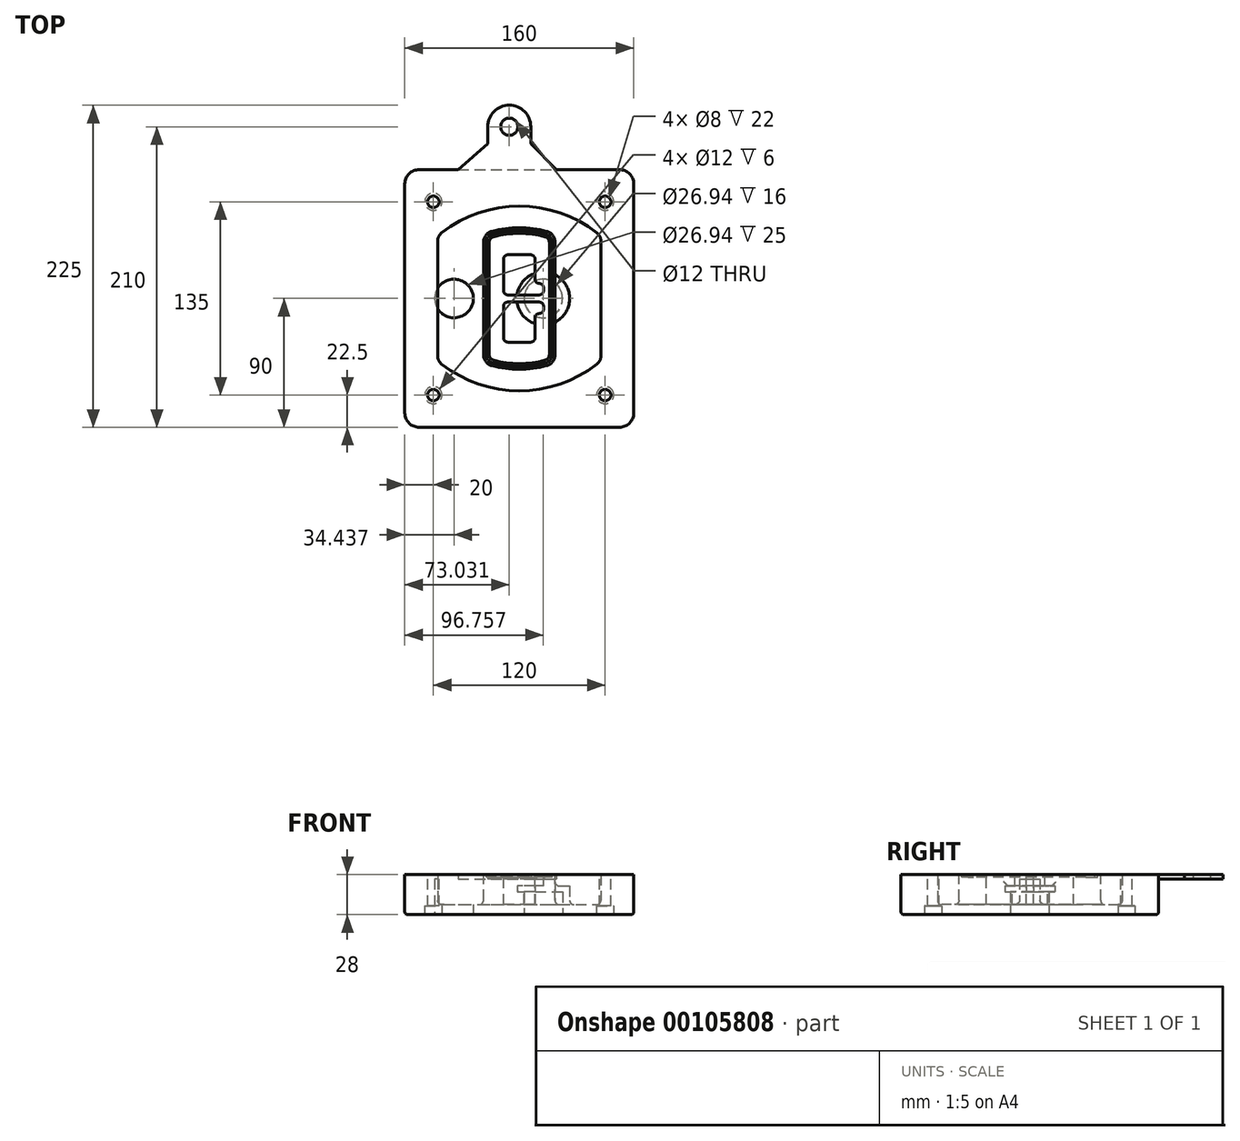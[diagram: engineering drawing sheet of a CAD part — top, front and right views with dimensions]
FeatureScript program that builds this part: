
annotation { "Feature Type Name" : "Feature", "Feature Type Description" : "" }
export const myFeature = defineFeature(function(context is Context, id is Id, definition is map)
    precondition{}
    {
        {
            var Q0;
            Q0=qCreatedBy(makeId("Top.planeOp"),FACE);
            var sketch = newSketch(context, id + "F0", { "sketchPlane" : qUnion([Q0])});
            skPoint(sketch, "E0.rect.middle", {"position": v(0, 0) * mm});
            skLineSegment(sketch, "E1.bottom", {"start": v(-70, -90) * mm, "end": v(70, -90) * mm});
            skLineSegment(sketch, "E1.top", {"start": v(-70, 90) * mm, "end": v(70, 90) * mm});
            skLineSegment(sketch, "E1.left", {"start": v(-80, -80) * mm, "end": v(-80, 80) * mm});
            skLineSegment(sketch, "E1.right", {"start": v(80, -80) * mm, "end": v(80, 80) * mm});
            skLineSegment(sketch, "E2", {"start": v(-80, 90) * mm, "end": v(80, -90) * mm, "construction": true});
            skLineSegment(sketch, "E3", {"start": v(80, 90) * mm, "end": v(-80, -90) * mm, "construction": true});
            skCircle(sketch, "E4", {"center": v(-60, 67.5) * mm, "radius": 4 * mm});
            skCircle(sketch, "E5", {"center": v(60, 67.5) * mm, "radius": 4 * mm});
            skCircle(sketch, "E6", {"center": v(60, -67.5) * mm, "radius": 4 * mm});
            skCircle(sketch, "E7", {"center": v(-60, -67.5) * mm, "radius": 4 * mm});
            skLineSegment(sketch, "E8", {"start": v(-60, 67.5) * mm, "end": v(60, 67.5) * mm, "construction": true});
            skLineSegment(sketch, "E9", {"start": v(60, 67.5) * mm, "end": v(60, -67.5) * mm, "construction": true});
            skLineSegment(sketch, "E10", {"start": v(60, -67.5) * mm, "end": v(-60, -67.5) * mm, "construction": true});
            skLineSegment(sketch, "E11", {"start": v(-60, -67.5) * mm, "end": v(-60, 67.5) * mm, "construction": true});
            skLineSegment(sketch, "E12", {"start": v(-60, 40.3) * mm, "end": v(-60, -40.3) * mm});
            skLineSegment(sketch, "E13", {"start": v(60, 40.3) * mm, "end": v(60, -40.3) * mm});
            skArc(sketch, "E14", {"start": v(56.15, 48.18) * mm, "mid": v(0, 67.5) * mm, "end": v(-56.15, 48.18) * mm});
            skArc(sketch, "E15", {"start": v(-56.15, -48.18) * mm, "mid": v(0, -67.5) * mm, "end": v(56.15, -48.18) * mm});
            skLineSegment(sketch, "E16", {"start": v(-60, 0) * mm, "end": v(60, 0) * mm, "construction": true});
            skPoint(sketch, "E17.visualSharp", {"position": v(-60, -45) * mm});
            skArc(sketch, "E17.filletArc", {"start": v(-60, -40.3) * mm, "mid": v(-58.99, -44.68) * mm, "end": v(-56.15, -48.18) * mm});
            skPoint(sketch, "E18.visualSharp", {"position": v(-60, 45) * mm});
            skArc(sketch, "E18.filletArc", {"start": v(-56.15, 48.18) * mm, "mid": v(-58.99, 44.68) * mm, "end": v(-60, 40.3) * mm});
            skPoint(sketch, "E19.visualSharp", {"position": v(60, 45) * mm});
            skArc(sketch, "E19.filletArc", {"start": v(60, 40.3) * mm, "mid": v(58.99, 44.68) * mm, "end": v(56.15, 48.18) * mm});
            skPoint(sketch, "E20.visualSharp", {"position": v(60, -45) * mm});
            skArc(sketch, "E20.filletArc", {"start": v(56.15, -48.18) * mm, "mid": v(58.99, -44.68) * mm, "end": v(60, -40.3) * mm});
            skPoint(sketch, "E21.visualSharp", {"position": v(-80, 90) * mm});
            skArc(sketch, "E21.filletArc", {"start": v(-70, 90) * mm, "mid": v(-77.07, 87.07) * mm, "end": v(-80, 80) * mm});
            skPoint(sketch, "E22.visualSharp", {"position": v(80, 90) * mm});
            skArc(sketch, "E22.filletArc", {"start": v(80, 80) * mm, "mid": v(77.07, 87.07) * mm, "end": v(70, 90) * mm});
            skPoint(sketch, "E23.visualSharp", {"position": v(80, -90) * mm});
            skArc(sketch, "E23.filletArc", {"start": v(70, -90) * mm, "mid": v(77.07, -87.07) * mm, "end": v(80, -80) * mm});
            skPoint(sketch, "E24.visualSharp", {"position": v(-80, -90) * mm});
            skArc(sketch, "E24.filletArc", {"start": v(-80, -80) * mm, "mid": v(-77.07, -87.07) * mm, "end": v(-70, -90) * mm});
            skArc(sketch, "E25.0", {"start": v(57, 40.3) * mm, "mid": v(56.3, 43.36) * mm, "end": v(54.3, 45.81) * mm});
            skLineSegment(sketch, "E25.1", {"start": v(57, 40.3) * mm, "end": v(57, -40.3) * mm});
            skArc(sketch, "E25.2", {"start": v(54.3, -45.81) * mm, "mid": v(56.3, -43.36) * mm, "end": v(57, -40.3) * mm});
            skArc(sketch, "E25.3", {"start": v(-54.3, -45.81) * mm, "mid": v(0, -64.5) * mm, "end": v(54.3, -45.81) * mm});
            skArc(sketch, "E25.4", {"start": v(-57, -40.3) * mm, "mid": v(-56.3, -43.36) * mm, "end": v(-54.3, -45.81) * mm});
            skArc(sketch, "E25.5", {"start": v(54.3, 45.81) * mm, "mid": v(0, 64.5) * mm, "end": v(-54.3, 45.81) * mm});
            skLineSegment(sketch, "E25.6", {"start": v(-57, 40.3) * mm, "end": v(-57, -40.3) * mm});
            skArc(sketch, "E25.7", {"start": v(-54.3, 45.81) * mm, "mid": v(-56.3, 43.36) * mm, "end": v(-57, 40.3) * mm});
            skArc(sketch, "E26.0", {"start": v(-58.62, 51.33) * mm, "mid": v(-62.58, 46.43) * mm, "end": v(-64, 40.3) * mm});
            skArc(sketch, "E26.1", {"start": v(58.62, 51.33) * mm, "mid": v(0, 71.5) * mm, "end": v(-58.62, 51.33) * mm});
            skArc(sketch, "E26.2", {"start": v(64, 40.3) * mm, "mid": v(62.58, 46.43) * mm, "end": v(58.62, 51.33) * mm});
            skLineSegment(sketch, "E26.3", {"start": v(64, 40.3) * mm, "end": v(64, -40.3) * mm});
            skArc(sketch, "E26.4", {"start": v(58.62, -51.33) * mm, "mid": v(62.58, -46.43) * mm, "end": v(64, -40.3) * mm});
            skLineSegment(sketch, "E26.5", {"start": v(-64, 40.3) * mm, "end": v(-64, -40.3) * mm});
            skArc(sketch, "E26.6", {"start": v(-58.62, -51.33) * mm, "mid": v(0, -71.5) * mm, "end": v(58.62, -51.33) * mm});
            skArc(sketch, "E26.7", {"start": v(-64, -40.3) * mm, "mid": v(-62.58, -46.43) * mm, "end": v(-58.62, -51.33) * mm});
            skSolve(sketch);
        }
        {
            var Q0;
            Q0=makeQuery(id+"F0.imprint","IMPRINT",FACE,{"disambiguationData":[TD([[makeQuery(id+"F0.imprint","IMPRINT",EDGE,{"derivedFrom":sQuery(id+"F0.wireOp",EDGE,"E1.bottom")}),1.0]])]});
            var Q1;
            Q1=makeQuery(id+"F0.imprint","IMPRINT",FACE,{"disambiguationData":[TD([[makeQuery(id+"F0.imprint","IMPRINT",EDGE,{"derivedFrom":sQuery(id+"F0.wireOp",EDGE,"E12")}),1.0]])]});
            var Q2;
            Q2=makeQuery(id+"F0.imprint","IMPRINT",FACE,{"disambiguationData":[TD([[makeQuery(id+"F0.imprint","IMPRINT",EDGE,{"derivedFrom":sQuery(id+"F0.wireOp",EDGE,"E25.0")}),1.0]])]});
            var Q3;
            Q3=makeQuery(id+"F0.imprint","IMPRINT",FACE,{"disambiguationData":[TD([[makeQuery(id+"F0.imprint","IMPRINT",EDGE,{"derivedFrom":sQuery(id+"F0.wireOp",EDGE,"E12")}),-1.0]])]});
            extrude(context, id + "F1", {"entities" : qUnion([Q0, Q1, Q2, Q3]), "oppositeDirection" : true, "depth" : 25 * mm});
        }
        {
            var Q0;
            Q0=makeQuery(id+"F0.imprint","IMPRINT",FACE,{"disambiguationData":[TD([[makeQuery(id+"F0.imprint","IMPRINT",EDGE,{"derivedFrom":sQuery(id+"F0.wireOp",EDGE,"E12")}),1.0]])]});
            extrude(context, id + "F2", {"entities" : qUnion([Q0]), "operationType" : NewBodyOperationType.ADD, "depth" : 3 * mm});
        }
        {
            var Q0;
            Q0=makeQuery(id+"F0.imprint","IMPRINT",FACE,{"disambiguationData":[TD([[makeQuery(id+"F0.imprint","IMPRINT",EDGE,{"derivedFrom":sQuery(id+"F0.wireOp",EDGE,"E25.0")}),1.0]])]});
            extrude(context, id + "F3", {"entities" : qUnion([Q0]), "operationType" : NewBodyOperationType.REMOVE, "oppositeDirection" : true, "depth" : 18 * mm});
        }
        {
            var Q0;
            Q0=makeQuery(id+"F2.opExtrude","CAP_FACE",FACE,{"disambiguationData":[OSD([sQuery(id+"F0.wireOp",EDGE,"E12"),sQuery(id+"F0.wireOp",EDGE,"E13"),sQuery(id+"F0.wireOp",EDGE,"E14"),sQuery(id+"F0.wireOp",EDGE,"E15"),sQuery(id+"F0.wireOp",EDGE,"E17.filletArc"),sQuery(id+"F0.wireOp",EDGE,"E18.filletArc"),sQuery(id+"F0.wireOp",EDGE,"E19.filletArc"),sQuery(id+"F0.wireOp",EDGE,"E20.filletArc"),sQuery(id+"F0.wireOp",EDGE,"E25.0"),sQuery(id+"F0.wireOp",EDGE,"E25.1"),sQuery(id+"F0.wireOp",EDGE,"E25.2"),sQuery(id+"F0.wireOp",EDGE,"E25.3"),sQuery(id+"F0.wireOp",EDGE,"E25.4"),sQuery(id+"F0.wireOp",EDGE,"E25.5"),sQuery(id+"F0.wireOp",EDGE,"E25.6"),sQuery(id+"F0.wireOp",EDGE,"E25.7")])],"isStart":false});
            var sketch = newSketch(context, id + "F4", { "sketchPlane" : qUnion([Q0])});
            skArc(sketch, "E27.0", {"start": v(-19.08, -46.97) * mm, "mid": v(0, -49.5) * mm, "end": v(19.08, -46.97) * mm});
            skArc(sketch, "E28.0", {"start": v(19.08, 46.97) * mm, "mid": v(0, 49.5) * mm, "end": v(-19.08, 46.97) * mm});
            skLineSegment(sketch, "E29", {"start": v(-25, 39.25) * mm, "end": v(-25, -39.25) * mm});
            skLineSegment(sketch, "E30", {"start": v(25, 39.25) * mm, "end": v(25, -39.25) * mm});
            skLineSegment(sketch, "E31", {"start": v(-25, 45.1) * mm, "end": v(25, 45.1) * mm, "construction": true});
            skLineSegment(sketch, "E32", {"start": v(-25, -45.1) * mm, "end": v(25, -45.1) * mm, "construction": true});
            skPoint(sketch, "E33.visualSharp", {"position": v(-25, 45.1) * mm});
            skArc(sketch, "E33.filletArc", {"start": v(-19.08, 46.97) * mm, "mid": v(-23.35, 44.11) * mm, "end": v(-25, 39.25) * mm});
            skPoint(sketch, "E34.visualSharp", {"position": v(25, 45.1) * mm});
            skArc(sketch, "E34.filletArc", {"start": v(25, 39.25) * mm, "mid": v(23.35, 44.11) * mm, "end": v(19.08, 46.97) * mm});
            skPoint(sketch, "E35.visualSharp", {"position": v(25, -45.1) * mm});
            skArc(sketch, "E35.filletArc", {"start": v(19.08, -46.97) * mm, "mid": v(23.35, -44.11) * mm, "end": v(25, -39.25) * mm});
            skPoint(sketch, "E36.visualSharp", {"position": v(-25, -45.1) * mm});
            skArc(sketch, "E36.filletArc", {"start": v(-25, -39.25) * mm, "mid": v(-23.35, -44.11) * mm, "end": v(-19.08, -46.97) * mm});
            skArc(sketch, "E37.0", {"start": v(54.3, 45.81) * mm, "mid": v(0, 64.5) * mm, "end": v(-54.3, 45.81) * mm});
            skArc(sketch, "E37.1", {"start": v(-54.3, 45.81) * mm, "mid": v(-56.3, 43.36) * mm, "end": v(-57, 40.3) * mm});
            skLineSegment(sketch, "E37.2", {"start": v(-57, 40.3) * mm, "end": v(-57, -40.3) * mm});
            skArc(sketch, "E37.3", {"start": v(-57, -40.3) * mm, "mid": v(-56.3, -43.36) * mm, "end": v(-54.3, -45.81) * mm});
            skArc(sketch, "E37.4", {"start": v(-54.3, -45.81) * mm, "mid": v(0, -64.5) * mm, "end": v(54.3, -45.81) * mm});
            skArc(sketch, "E37.5", {"start": v(54.3, -45.81) * mm, "mid": v(56.3, -43.36) * mm, "end": v(57, -40.3) * mm});
            skLineSegment(sketch, "E37.6", {"start": v(57, 40.3) * mm, "end": v(57, -40.3) * mm});
            skArc(sketch, "E37.7", {"start": v(57, 40.3) * mm, "mid": v(56.3, 43.36) * mm, "end": v(54.3, 45.81) * mm});
            skLineSegment(sketch, "E38.0", {"start": v(23, 39.25) * mm, "end": v(23, -39.25) * mm});
            skArc(sketch, "E38.1", {"start": v(18.56, -45.04) * mm, "mid": v(21.76, -42.9) * mm, "end": v(23, -39.25) * mm});
            skArc(sketch, "E38.2", {"start": v(-18.56, -45.04) * mm, "mid": v(0, -47.5) * mm, "end": v(18.56, -45.04) * mm});
            skArc(sketch, "E38.3", {"start": v(-23, -39.25) * mm, "mid": v(-21.76, -42.9) * mm, "end": v(-18.56, -45.04) * mm});
            skLineSegment(sketch, "E38.4", {"start": v(-23, 39.25) * mm, "end": v(-23, -39.25) * mm});
            skArc(sketch, "E38.5", {"start": v(23, 39.25) * mm, "mid": v(21.76, 42.9) * mm, "end": v(18.56, 45.04) * mm});
            skArc(sketch, "E38.6", {"start": v(-18.56, 45.04) * mm, "mid": v(-21.76, 42.9) * mm, "end": v(-23, 39.25) * mm});
            skArc(sketch, "E38.7", {"start": v(18.56, 45.04) * mm, "mid": v(0, 47.5) * mm, "end": v(-18.56, 45.04) * mm});
            skArc(sketch, "E39.0", {"start": v(21, 39.25) * mm, "mid": v(20.18, 41.68) * mm, "end": v(18.04, 43.1) * mm});
            skLineSegment(sketch, "E39.1", {"start": v(21, 39.25) * mm, "end": v(21, -39.25) * mm});
            skArc(sketch, "E39.2", {"start": v(18.04, -43.1) * mm, "mid": v(20.18, -41.68) * mm, "end": v(21, -39.25) * mm});
            skArc(sketch, "E39.3", {"start": v(-18.04, -43.1) * mm, "mid": v(0, -45.5) * mm, "end": v(18.04, -43.1) * mm});
            skArc(sketch, "E39.4", {"start": v(-21, -39.25) * mm, "mid": v(-20.18, -41.68) * mm, "end": v(-18.04, -43.1) * mm});
            skArc(sketch, "E39.5", {"start": v(18.04, 43.1) * mm, "mid": v(0, 45.5) * mm, "end": v(-18.04, 43.1) * mm});
            skLineSegment(sketch, "E39.6", {"start": v(-21, 39.25) * mm, "end": v(-21, -39.25) * mm});
            skArc(sketch, "E39.7", {"start": v(-18.04, 43.1) * mm, "mid": v(-20.18, 41.68) * mm, "end": v(-21, 39.25) * mm});
            skLineSegment(sketch, "E40", {"start": v(-25, 0) * mm, "end": v(25, 0) * mm, "construction": true});
            skLineSegment(sketch, "E41", {"start": v(-11, 5.5) * mm, "end": v(-11, 27.5) * mm});
            skLineSegment(sketch, "E42", {"start": v(-8, 30.5) * mm, "end": v(8, 30.5) * mm});
            skLineSegment(sketch, "E43", {"start": v(11, 27.5) * mm, "end": v(11, 13.5) * mm});
            skLineSegment(sketch, "E44", {"start": v(14, 10.5) * mm, "end": v(14, 10.5) * mm});
            skLineSegment(sketch, "E45", {"start": v(17, 7.5) * mm, "end": v(17, 5.5) * mm});
            skLineSegment(sketch, "E46", {"start": v(14, 2.5) * mm, "end": v(-8, 2.5) * mm});
            skPoint(sketch, "E47.visualSharp", {"position": v(-11, 30.5) * mm});
            skArc(sketch, "E47.filletArc", {"start": v(-8, 30.5) * mm, "mid": v(-10.12, 29.62) * mm, "end": v(-11, 27.5) * mm});
            skPoint(sketch, "E48.visualSharp", {"position": v(11, 30.5) * mm});
            skArc(sketch, "E48.filletArc", {"start": v(11, 27.5) * mm, "mid": v(10.12, 29.62) * mm, "end": v(8, 30.5) * mm});
            skPoint(sketch, "E49.visualSharp", {"position": v(11, 10.5) * mm});
            skArc(sketch, "E49.filletArc", {"start": v(11, 13.5) * mm, "mid": v(11.88, 11.38) * mm, "end": v(14, 10.5) * mm});
            skPoint(sketch, "E50.visualSharp", {"position": v(17, 10.5) * mm});
            skArc(sketch, "E50.filletArc", {"start": v(17, 7.5) * mm, "mid": v(16.12, 9.62) * mm, "end": v(14, 10.5) * mm});
            skPoint(sketch, "E51.visualSharp", {"position": v(17, 2.5) * mm});
            skArc(sketch, "E51.filletArc", {"start": v(14, 2.5) * mm, "mid": v(16.12, 3.38) * mm, "end": v(17, 5.5) * mm});
            skPoint(sketch, "E52.visualSharp", {"position": v(-11, 2.5) * mm});
            skArc(sketch, "E52.filletArc", {"start": v(-11, 5.5) * mm, "mid": v(-10.12, 3.38) * mm, "end": v(-8, 2.5) * mm});
            skLineSegment(sketch, "E53.0.MirrorCS", {"start": v(14, -2.5) * mm, "end": v(-8, -2.5) * mm});
            skArc(sketch, "E54.0.MirrorCS", {"start": v(-11, -5.5) * mm, "mid": v(-10.12, -3.38) * mm, "end": v(-8, -2.5) * mm});
            skLineSegment(sketch, "E55.0.MirrorCS", {"start": v(-11, -5.5) * mm, "end": v(-11, -27.5) * mm});
            skArc(sketch, "E56.0.MirrorCS", {"start": v(-8, -30.5) * mm, "mid": v(-10.12, -29.62) * mm, "end": v(-11, -27.5) * mm});
            skLineSegment(sketch, "E57.0.MirrorCS", {"start": v(-8, -30.5) * mm, "end": v(8, -30.5) * mm});
            skArc(sketch, "E58.0.MirrorCS", {"start": v(11, -27.5) * mm, "mid": v(10.12, -29.62) * mm, "end": v(8, -30.5) * mm});
            skLineSegment(sketch, "E59.0.MirrorCS", {"start": v(11, -27.5) * mm, "end": v(11, -13.5) * mm});
            skArc(sketch, "E60.0.MirrorCS", {"start": v(11, -13.5) * mm, "mid": v(11.88, -11.38) * mm, "end": v(14, -10.5) * mm});
            skArc(sketch, "E61.0.MirrorCS", {"start": v(17, -7.5) * mm, "mid": v(16.12, -9.62) * mm, "end": v(14, -10.5) * mm});
            skLineSegment(sketch, "E62.0.MirrorCS", {"start": v(17, -7.5) * mm, "end": v(17, -5.5) * mm});
            skArc(sketch, "E63.0.MirrorCS", {"start": v(14, -2.5) * mm, "mid": v(16.12, -3.38) * mm, "end": v(17, -5.5) * mm});
            skSolve(sketch);
        }
        {
            var Q0;
            Q0=makeQuery(id+"F4.imprint","IMPRINT",FACE,{"disambiguationData":[TD([[makeQuery(id+"F4.imprint","IMPRINT",EDGE,{"derivedFrom":sQuery(id+"F4.wireOp",EDGE,"E27.0")}),1.0]])]});
            var Q1;
            Q1=makeQuery(id+"F4.imprint","IMPRINT",FACE,{"disambiguationData":[TD([[makeQuery(id+"F4.imprint","IMPRINT",EDGE,{"derivedFrom":sQuery(id+"F4.wireOp",EDGE,"E38.0")}),-1.0]])]});
            var Q2;
            Q2=makeQuery(id+"F4.imprint","IMPRINT",FACE,{"disambiguationData":[TD([[makeQuery(id+"F4.imprint","IMPRINT",EDGE,{"derivedFrom":sQuery(id+"F4.wireOp",EDGE,"E39.0")}),1.0]])]});
            extrude(context, id + "F5", {"entities" : qUnion([Q0, Q1, Q2]), "operationType" : NewBodyOperationType.ADD, "endBound" : BoundingType.UP_TO_NEXT, "oppositeDirection" : true, "depth" : 25 * mm});
        }
        {
            var Q0;
            Q0=makeQuery(id+"F4.imprint","IMPRINT",FACE,{"disambiguationData":[TD([[makeQuery(id+"F4.imprint","IMPRINT",EDGE,{"derivedFrom":sQuery(id+"F4.wireOp",EDGE,"E38.0")}),-1.0]])]});
            extrude(context, id + "F6", {"entities" : qUnion([Q0]), "operationType" : NewBodyOperationType.REMOVE, "oppositeDirection" : true, "depth" : 2 * mm});
        }
        {
            var Q0;
            Q0=makeQuery(id+"F1.opExtrude","CAP_FACE",FACE,{"disambiguationData":[OSD([sQuery(id+"F0.wireOp",EDGE,"E1.bottom"),sQuery(id+"F0.wireOp",EDGE,"E1.top"),sQuery(id+"F0.wireOp",EDGE,"E1.left"),sQuery(id+"F0.wireOp",EDGE,"E1.right"),sQuery(id+"F0.wireOp",EDGE,"E4"),sQuery(id+"F0.wireOp",EDGE,"E5"),sQuery(id+"F0.wireOp",EDGE,"E6"),sQuery(id+"F0.wireOp",EDGE,"E7"),sQuery(id+"F0.wireOp",EDGE,"E21.filletArc"),sQuery(id+"F0.wireOp",EDGE,"E22.filletArc"),sQuery(id+"F0.wireOp",EDGE,"E23.filletArc"),sQuery(id+"F0.wireOp",EDGE,"E24.filletArc")])],"isStart":false});
            var sketch = newSketch(context, id + "F7", { "sketchPlane" : qUnion([Q0])});
            skCircle(sketch, "E64", {"center": v(16.76, 0) * mm, "radius": 13.47 * mm});
            skCircle(sketch, "E65", {"center": v(-45.56, 0) * mm, "radius": 13.47 * mm});
            skLineSegment(sketch, "E66", {"start": v(80, 0) * mm, "end": v(-80, 0) * mm});
            skCircle(sketch, "E67", {"center": v(16.76, 0) * mm, "radius": 18.47 * mm});
            skCircle(sketch, "E68", {"center": v(60, -67.5) * mm, "radius": 6 * mm});
            skCircle(sketch, "E69", {"center": v(-60, -67.5) * mm, "radius": 6 * mm});
            skCircle(sketch, "E70", {"center": v(-60, 67.5) * mm, "radius": 6 * mm});
            skCircle(sketch, "E71", {"center": v(60, 67.5) * mm, "radius": 6 * mm});
            skSolve(sketch);
        }
        {
            var Q0;
            {var subQ1=sQuery(id+"F7.wireOp",EDGE,"E66");var subQ4=sQuery(id+"F7.wireOp",EDGE,"E64");var subQ6=makeQuery(id+"F7.imprint","INTERSECT",VERTEX,{"disambiguationData":[OD(0.0)],"derivedFrom":[subQ4,subQ1]});Q0=makeQuery(id+"F7.imprint","IMPRINT",FACE,{"disambiguationData":[TD([[makeQuery(id+"F7.imprint","IMPRINT",EDGE,{"disambiguationData":[TD([[subQ6,-1.0]])],"derivedFrom":subQ4}),-1.0]])]});}
            var Q1;
            {var subQ0=sQuery(id+"F7.wireOp",EDGE,"E66");var subQ1=sQuery(id+"F7.wireOp",EDGE,"E64");var subQ3=makeQuery(id+"F7.imprint","INTERSECT",VERTEX,{"disambiguationData":[OD(0.0)],"derivedFrom":[subQ1,subQ0]});Q1=makeQuery(id+"F7.imprint","IMPRINT",FACE,{"disambiguationData":[TD([[makeQuery(id+"F7.imprint","IMPRINT",EDGE,{"disambiguationData":[TD([[subQ3,-1.0]])],"derivedFrom":subQ1}),1.0]])]});}
            var Q2;
            {var subQ0=sQuery(id+"F7.wireOp",EDGE,"E66");var subQ1=sQuery(id+"F7.wireOp",EDGE,"E64");var subQ3=makeQuery(id+"F7.imprint","INTERSECT",VERTEX,{"disambiguationData":[OD(0.0)],"derivedFrom":[subQ1,subQ0]});Q2=makeQuery(id+"F7.imprint","IMPRINT",FACE,{"disambiguationData":[TD([[makeQuery(id+"F7.imprint","IMPRINT",EDGE,{"disambiguationData":[TD([[subQ3,1.0]])],"derivedFrom":subQ1}),1.0]])]});}
            var Q3;
            {var subQ1=sQuery(id+"F7.wireOp",EDGE,"E66");var subQ4=sQuery(id+"F7.wireOp",EDGE,"E64");var subQ6=makeQuery(id+"F7.imprint","INTERSECT",VERTEX,{"disambiguationData":[OD(0.0)],"derivedFrom":[subQ4,subQ1]});Q3=makeQuery(id+"F7.imprint","IMPRINT",FACE,{"disambiguationData":[TD([[makeQuery(id+"F7.imprint","IMPRINT",EDGE,{"disambiguationData":[TD([[subQ6,1.0]])],"derivedFrom":subQ4}),-1.0]])]});}
            extrude(context, id + "F8", {"entities" : qUnion([Q0, Q1, Q2, Q3]), "operationType" : NewBodyOperationType.ADD, "oppositeDirection" : true, "depth" : 20 * mm});
        }
        {
            var Q0;
            {var subQ0=sQuery(id+"F7.wireOp",EDGE,"E66");var subQ1=sQuery(id+"F7.wireOp",EDGE,"E64");var subQ3=makeQuery(id+"F7.imprint","INTERSECT",VERTEX,{"disambiguationData":[OD(0.0)],"derivedFrom":[subQ1,subQ0]});Q0=makeQuery(id+"F7.imprint","IMPRINT",FACE,{"disambiguationData":[TD([[makeQuery(id+"F7.imprint","IMPRINT",EDGE,{"disambiguationData":[TD([[subQ3,-1.0]])],"derivedFrom":subQ1}),1.0]])]});}
            var Q1;
            {var subQ0=sQuery(id+"F7.wireOp",EDGE,"E66");var subQ1=sQuery(id+"F7.wireOp",EDGE,"E64");var subQ3=makeQuery(id+"F7.imprint","INTERSECT",VERTEX,{"disambiguationData":[OD(0.0)],"derivedFrom":[subQ1,subQ0]});Q1=makeQuery(id+"F7.imprint","IMPRINT",FACE,{"disambiguationData":[TD([[makeQuery(id+"F7.imprint","IMPRINT",EDGE,{"disambiguationData":[TD([[subQ3,1.0]])],"derivedFrom":subQ1}),1.0]])]});}
            extrude(context, id + "F9", {"entities" : qUnion([Q0, Q1]), "operationType" : NewBodyOperationType.REMOVE, "oppositeDirection" : true, "depth" : 16 * mm});
        }
        {
            var Q0;
            {var subQ0=sQuery(id+"F7.wireOp",EDGE,"E66");var subQ1=sQuery(id+"F7.wireOp",EDGE,"E65");var subQ3=makeQuery(id+"F7.imprint","INTERSECT",VERTEX,{"disambiguationData":[OD(0.0)],"derivedFrom":[subQ1,subQ0]});Q0=makeQuery(id+"F7.imprint","IMPRINT",FACE,{"disambiguationData":[TD([[makeQuery(id+"F7.imprint","IMPRINT",EDGE,{"disambiguationData":[TD([[subQ3,-1.0]])],"derivedFrom":subQ1}),1.0]])]});}
            var Q1;
            {var subQ0=sQuery(id+"F7.wireOp",EDGE,"E66");var subQ1=sQuery(id+"F7.wireOp",EDGE,"E65");var subQ3=makeQuery(id+"F7.imprint","INTERSECT",VERTEX,{"disambiguationData":[OD(0.0)],"derivedFrom":[subQ1,subQ0]});Q1=makeQuery(id+"F7.imprint","IMPRINT",FACE,{"disambiguationData":[TD([[makeQuery(id+"F7.imprint","IMPRINT",EDGE,{"disambiguationData":[TD([[subQ3,1.0]])],"derivedFrom":subQ1}),1.0]])]});}
            extrude(context, id + "F10", {"entities" : qUnion([Q0, Q1]), "operationType" : NewBodyOperationType.REMOVE, "oppositeDirection" : true, "depth" : 25 * mm});
        }
        {
            var Q0;
            Q0=makeQuery(id+"F7.imprint","IMPRINT",FACE,{"disambiguationData":[TD([[makeQuery(id+"F7.imprint","IMPRINT",EDGE,{"derivedFrom":sQuery(id+"F7.wireOp",EDGE,"E68")}),1.0]])]});
            var Q1;
            Q1=makeQuery(id+"F7.imprint","IMPRINT",FACE,{"disambiguationData":[TD([[makeQuery(id+"F7.imprint","IMPRINT",EDGE,{"derivedFrom":makeQuery(id+"F1.opExtrude","CAP_EDGE",EDGE,{"disambiguationData":[OSD([sQuery(id+"F0.wireOp",EDGE,"E5")])],"isStart":false})}),-1.0]])]});
            var Q2;
            Q2=makeQuery(id+"F7.imprint","IMPRINT",FACE,{"disambiguationData":[TD([[makeQuery(id+"F7.imprint","IMPRINT",EDGE,{"derivedFrom":sQuery(id+"F7.wireOp",EDGE,"E69")}),1.0]])]});
            var Q3;
            Q3=makeQuery(id+"F7.imprint","IMPRINT",FACE,{"disambiguationData":[TD([[makeQuery(id+"F7.imprint","IMPRINT",EDGE,{"derivedFrom":makeQuery(id+"F1.opExtrude","CAP_EDGE",EDGE,{"disambiguationData":[OSD([sQuery(id+"F0.wireOp",EDGE,"E4")])],"isStart":false})}),-1.0]])]});
            var Q4;
            Q4=makeQuery(id+"F7.imprint","IMPRINT",FACE,{"disambiguationData":[TD([[makeQuery(id+"F7.imprint","IMPRINT",EDGE,{"derivedFrom":sQuery(id+"F7.wireOp",EDGE,"E70")}),1.0]])]});
            var Q5;
            Q5=makeQuery(id+"F7.imprint","IMPRINT",FACE,{"disambiguationData":[TD([[makeQuery(id+"F7.imprint","IMPRINT",EDGE,{"derivedFrom":makeQuery(id+"F1.opExtrude","CAP_EDGE",EDGE,{"disambiguationData":[OSD([sQuery(id+"F0.wireOp",EDGE,"E7")])],"isStart":false})}),-1.0]])]});
            var Q6;
            Q6=makeQuery(id+"F7.imprint","IMPRINT",FACE,{"disambiguationData":[TD([[makeQuery(id+"F7.imprint","IMPRINT",EDGE,{"derivedFrom":sQuery(id+"F7.wireOp",EDGE,"E71")}),1.0]])]});
            var Q7;
            Q7=makeQuery(id+"F7.imprint","IMPRINT",FACE,{"disambiguationData":[TD([[makeQuery(id+"F7.imprint","IMPRINT",EDGE,{"derivedFrom":makeQuery(id+"F1.opExtrude","CAP_EDGE",EDGE,{"disambiguationData":[OSD([sQuery(id+"F0.wireOp",EDGE,"E6")])],"isStart":false})}),-1.0]])]});
            extrude(context, id + "F11", {"entities" : qUnion([Q0, Q1, Q2, Q3, Q4, Q5, Q6, Q7]), "operationType" : NewBodyOperationType.REMOVE, "oppositeDirection" : true, "depth" : 6 * mm});
        }
        {
            var Q0;
            Q0=makeQuery(id+"F9.boolean.opBoolean","COPY",FACE,{"derivedFrom":makeQuery(id+"F9.opExtrude","CAP_FACE",FACE,{"disambiguationData":[OSD([sQuery(id+"F7.wireOp",EDGE,"E64")])],"isStart":false})});
            var sketch = newSketch(context, id + "F12", { "sketchPlane" : qUnion([Q0])});
            skArc(sketch, "E72.0", {"start": v(11, 17.55) * mm, "mid": v(2.57, 11.82) * mm, "end": v(-1.54, 2.5) * mm});
            skArc(sketch, "E72.1", {"start": v(-1.54, -2.5) * mm, "mid": v(2.57, -11.82) * mm, "end": v(11, -17.55) * mm});
            skLineSegment(sketch, "E73", {"start": v(-1.54, -2.5) * mm, "end": v(14, -2.5) * mm});
            skLineSegment(sketch, "E74.0", {"start": v(14, 2.5) * mm, "end": v(-1.54, 2.5) * mm});
            skArc(sketch, "E74.1", {"start": v(14, 2.5) * mm, "mid": v(16.12, 3.38) * mm, "end": v(17, 5.5) * mm});
            skLineSegment(sketch, "E74.2", {"start": v(17, 7.5) * mm, "end": v(17, 5.5) * mm});
            skArc(sketch, "E74.3", {"start": v(17, 7.5) * mm, "mid": v(16.12, 9.62) * mm, "end": v(14, 10.5) * mm});
            skArc(sketch, "E74.4", {"start": v(11, 13.5) * mm, "mid": v(11.88, 11.38) * mm, "end": v(14, 10.5) * mm});
            skLineSegment(sketch, "E74.5", {"start": v(11, 17.55) * mm, "end": v(11, 13.5) * mm});
            skLineSegment(sketch, "E74.7", {"start": v(14, -2.5) * mm, "end": v(-1.54, -2.5) * mm});
            skArc(sketch, "E74.8", {"start": v(14, -2.5) * mm, "mid": v(16.12, -3.38) * mm, "end": v(17, -5.5) * mm});
            skLineSegment(sketch, "E74.9", {"start": v(17, -7.5) * mm, "end": v(17, -5.5) * mm});
            skArc(sketch, "E74.10", {"start": v(17, -7.5) * mm, "mid": v(16.12, -9.62) * mm, "end": v(14, -10.5) * mm});
            skArc(sketch, "E74.11", {"start": v(11, -13.5) * mm, "mid": v(11.88, -11.38) * mm, "end": v(14, -10.5) * mm});
            skLineSegment(sketch, "E74.12", {"start": v(11, -17.55) * mm, "end": v(11, -13.5) * mm});
            skPoint(sketch, "E75.orphan", {"position": v(11, -27.5) * mm});
            skPoint(sketch, "E76.orphan", {"position": v(-8, -2.5) * mm});
            skPoint(sketch, "E77.orphan", {"position": v(-8, 2.5) * mm});
            skPoint(sketch, "E78.orphan", {"position": v(11, 27.5) * mm});
            skSolve(sketch);
        }
        {
            var Q0;
            {var subQ7=sQuery(id+"F12.wireOp",EDGE,"E72.0");var subQ14=sQuery(id+"F12.wireOp",EDGE,"E72.1");var subQ16=sQuery(id+"F12.wireOp",EDGE,"E74.1");var subQ18=sQuery(id+"F12.wireOp",EDGE,"E74.8");Q0=qUnion([makeQuery(id+"F12.imprint","IMPRINT",FACE,{"disambiguationData":[TD([[makeQuery(id+"F12.imprint","IMPRINT",EDGE,{"derivedFrom":subQ7}),1.0]])]}),makeQuery(id+"F12.imprint","IMPRINT",FACE,{"disambiguationData":[TD([[makeQuery(id+"F12.imprint","IMPRINT",EDGE,{"derivedFrom":subQ14}),1.0]])]}),makeQuery(id+"F12.imprint","IMPRINT",FACE,{"disambiguationData":[TD([[makeQuery(id+"F12.imprint","IMPRINT",EDGE,{"derivedFrom":subQ16}),1.0]])]}),makeQuery(id+"F12.imprint","IMPRINT",FACE,{"disambiguationData":[TD([[makeQuery(id+"F12.imprint","IMPRINT",EDGE,{"derivedFrom":subQ18}),-1.0]])]})]);}
            var Q1;
            Q1=makeQuery(id+"F5.boolean.opBoolean","SPLIT",FACE,{"disambiguationData":[TD([makeQuery(id+"F5.opExtrude","SWEPT_FACE",FACE,{"disambiguationData":[OSD([sQuery(id+"F4.wireOp",EDGE,"E41")])]})])],"derivedFrom":makeQuery(id+"F3.boolean.opBoolean","COPY",FACE,{"derivedFrom":makeQuery(id+"F3.opExtrude","CAP_FACE",FACE,{"disambiguationData":[OSD([sQuery(id+"F0.wireOp",EDGE,"E25.0"),sQuery(id+"F0.wireOp",EDGE,"E25.1"),sQuery(id+"F0.wireOp",EDGE,"E25.2"),sQuery(id+"F0.wireOp",EDGE,"E25.3"),sQuery(id+"F0.wireOp",EDGE,"E25.4"),sQuery(id+"F0.wireOp",EDGE,"E25.5"),sQuery(id+"F0.wireOp",EDGE,"E25.6"),sQuery(id+"F0.wireOp",EDGE,"E25.7")])],"isStart":false})})});
            extrude(context, id + "F13", {"entities" : qUnion([Q0]), "operationType" : NewBodyOperationType.REMOVE, "endBound" : BoundingType.UP_TO_SURFACE, "endBoundEntityFace" : qUnion([Q1]), "depth" : 25 * mm});
        }
        {
            var Q0;
            Q0=makeQuery(id+"F3.boolean.opBoolean","COPY",EDGE,{"derivedFrom":makeQuery(id+"F3.opExtrude","CAP_EDGE",EDGE,{"disambiguationData":[OSD([sQuery(id+"F0.wireOp",EDGE,"E25.6")])],"isStart":false})});
            var Q1;
            Q1=makeQuery(id+"F8.boolean.opBoolean","INTERSECT",EDGE,{"derivedFrom":[makeQuery(id+"F5.opExtrude","SWEPT_FACE",FACE,{"disambiguationData":[OSD([sQuery(id+"F4.wireOp",EDGE,"E30")])]}),makeQuery(id+"F8.opExtrude","CAP_FACE",FACE,{"disambiguationData":[OSD([sQuery(id+"F7.wireOp",EDGE,"E67")])],"isStart":false})]});
            var Q2;
            Q2=makeQuery(id+"F8.boolean.opBoolean","INTERSECT",EDGE,{"disambiguationData":[OD(1.0)],"derivedFrom":[makeQuery(id+"F5.opExtrude","SWEPT_FACE",FACE,{"disambiguationData":[OSD([sQuery(id+"F4.wireOp",EDGE,"E30")])]}),makeQuery(id+"F8.opExtrude","SWEPT_FACE",FACE,{"disambiguationData":[OSD([sQuery(id+"F7.wireOp",EDGE,"E67")])]})]});
            var Q3;
            {var subQ0=sQuery(id+"F4.wireOp",EDGE,"E30");Q3=makeQuery(id+"F8.boolean.opBoolean","SPLIT",EDGE,{"disambiguationData":[TD([makeQuery(id+"F5.opExtrude","SWEPT_FACE",FACE,{"disambiguationData":[OSD([sQuery(id+"F4.wireOp",EDGE,"E35.filletArc")])]})])],"derivedFrom":makeQuery(id+"F5.opExtrude","CAP_EDGE",EDGE,{"disambiguationData":[OSD([subQ0])],"isStart":false})});}
            var Q4;
            {var subQ0=sQuery(id+"F0.wireOp",EDGE,"E25.7");var subQ1=sQuery(id+"F0.wireOp",EDGE,"E25.1");var subQ2=sQuery(id+"F0.wireOp",EDGE,"E25.6");var subQ3=sQuery(id+"F0.wireOp",EDGE,"E25.5");var subQ4=sQuery(id+"F0.wireOp",EDGE,"E25.4");var subQ5=sQuery(id+"F0.wireOp",EDGE,"E25.0");var subQ6=sQuery(id+"F0.wireOp",EDGE,"E25.2");var subQ7=sQuery(id+"F0.wireOp",EDGE,"E25.3");Q4=makeQuery(id+"F8.boolean.opBoolean","INTERSECT",EDGE,{"derivedFrom":[makeQuery(id+"F5.boolean.opBoolean","SPLIT",FACE,{"disambiguationData":[TD([makeQuery(id+"F2.opExtrude","SWEPT_FACE",FACE,{"disambiguationData":[OSD([subQ5])]})])],"derivedFrom":makeQuery(id+"F3.boolean.opBoolean","COPY",FACE,{"derivedFrom":makeQuery(id+"F3.opExtrude","CAP_FACE",FACE,{"disambiguationData":[OSD([subQ5,subQ1,subQ6,subQ7,subQ4,subQ3,subQ2,subQ0])],"isStart":false})})}),makeQuery(id+"F8.opExtrude","SWEPT_FACE",FACE,{"disambiguationData":[OSD([sQuery(id+"F7.wireOp",EDGE,"E67")])]})]});}
            var Q5;
            Q5=makeQuery(id+"F8.boolean.opBoolean","INTERSECT",EDGE,{"disambiguationData":[OD(0.0)],"derivedFrom":[makeQuery(id+"F5.opExtrude","SWEPT_FACE",FACE,{"disambiguationData":[OSD([sQuery(id+"F4.wireOp",EDGE,"E30")])]}),makeQuery(id+"F8.opExtrude","SWEPT_FACE",FACE,{"disambiguationData":[OSD([sQuery(id+"F7.wireOp",EDGE,"E67")])]})]});
            fillet(context, id + "F14", {"entities" : qUnion([Q0, Q1, Q2, Q3, Q4, Q5]), "radius" : 3 * mm, "tangentPropagation" : true, "allowEdgeOverflow" : false});
        }
        {
            var Q0;
            Q0=makeQuery(id+"F1.opExtrude","CAP_EDGE",EDGE,{"disambiguationData":[OSD([sQuery(id+"F0.wireOp",EDGE,"E1.bottom")])],"isStart":false});
            fillet(context, id + "F15", {"entities" : qUnion([Q0]), "radius" : 2 * mm, "tangentPropagation" : true, "allowEdgeOverflow" : false});
        }
        {
            var Q0;
            {var subQ0=sQuery(id+"F0.wireOp",EDGE,"E22.filletArc");var subQ1=sQuery(id+"F0.wireOp",EDGE,"E7");var subQ2=sQuery(id+"F0.wireOp",EDGE,"E6");var subQ3=sQuery(id+"F0.wireOp",EDGE,"E5");var subQ4=sQuery(id+"F0.wireOp",EDGE,"E4");var subQ5=sQuery(id+"F0.wireOp",EDGE,"E1.bottom");var subQ6=sQuery(id+"F0.wireOp",EDGE,"E21.filletArc");var subQ7=sQuery(id+"F0.wireOp",EDGE,"E1.top");var subQ8=sQuery(id+"F0.wireOp",EDGE,"E1.left");var subQ9=sQuery(id+"F0.wireOp",EDGE,"E1.right");var subQ10=sQuery(id+"F0.wireOp",EDGE,"E23.filletArc");var subQ11=sQuery(id+"F0.wireOp",EDGE,"E24.filletArc");Q0=makeQuery(id+"F2.boolean.opBoolean","SPLIT",FACE,{"disambiguationData":[TD([makeQuery(id+"F1.opExtrude","SWEPT_FACE",FACE,{"disambiguationData":[OSD([subQ5])]})])],"derivedFrom":makeQuery(id+"F1.opExtrude","CAP_FACE",FACE,{"disambiguationData":[OSD([subQ5,subQ7,subQ8,subQ9,subQ4,subQ3,subQ2,subQ1,subQ6,subQ0,subQ10,subQ11])],"isStart":true})});}
            var sketch = newSketch(context, id + "F16", { "sketchPlane" : qUnion([Q0])});
            skPoint(sketch, "E79.endSnap0", {"position": v(0, 90) * mm});
            skLineSegment(sketch, "E80", {"start": v(-42.73, 90) * mm, "end": v(-21.97, 108) * mm});
            skLineSegment(sketch, "E81", {"start": v(-21.97, 108) * mm, "end": v(-21.97, 120) * mm});
            skArc(sketch, "E82", {"start": v(8.03, 120) * mm, "mid": v(-6.97, 135) * mm, "end": v(-21.97, 120) * mm});
            skLineSegment(sketch, "E83", {"start": v(8.03, 120) * mm, "end": v(8.03, 108) * mm});
            skLineSegment(sketch, "E84", {"start": v(8.03, 108) * mm, "end": v(25.94, 90) * mm});
            skCircle(sketch, "E85", {"center": v(-6.97, 120) * mm, "radius": 6 * mm});
            skLineSegment(sketch, "E86", {"start": v(0, 0) * mm, "end": v(80, 0) * mm});
            skLineSegment(sketch, "E87", {"start": v(80, 0) * mm, "end": v(-80, 0) * mm});
            skArc(sketch, "E88.MirrorCS", {"start": v(8.03, -120) * mm, "mid": v(-6.97, -135) * mm, "end": v(-21.97, -120) * mm});
            skLineSegment(sketch, "E89.MirrorCS", {"start": v(8.03, -120) * mm, "end": v(8.03, -108) * mm});
            skLineSegment(sketch, "E90.MirrorCS", {"start": v(-21.97, -108) * mm, "end": v(-21.97, -120) * mm});
            skLineSegment(sketch, "E91.MirrorCS", {"start": v(-42.73, -90) * mm, "end": v(-21.97, -108) * mm});
            skLineSegment(sketch, "E92.MirrorCS", {"start": v(8.03, -108) * mm, "end": v(25.94, -90) * mm});
            skCircle(sketch, "E93.MirrorC", {"center": v(-6.97, -120) * mm, "radius": 6 * mm});
            skLineSegment(sketch, "E94", {"start": v(-6.97, 120) * mm, "end": v(-6.97, 90) * mm, "construction": true});
            skLineSegment(sketch, "E95", {"start": v(-6.97, -120) * mm, "end": v(-6.97, -90) * mm, "construction": true});
            skSolve(sketch);
        }
        {
            var Q0;
            {var subQ0=sQuery(id+"F16.wireOp",EDGE,"E80");Q0=makeQuery(id+"F16.imprint","IMPRINT",FACE,{"disambiguationData":[TD([[makeQuery(id+"F16.imprint","IMPRINT",EDGE,{"derivedFrom":subQ0}),-1.0]])]});}
            var Q1;
            Q1=makeQuery(id+"F16.imprint","IMPRINT",FACE,{"disambiguationData":[TD([[makeQuery(id+"F16.imprint","IMPRINT",EDGE,{"derivedFrom":sQuery(id+"F16.wireOp",EDGE,"E88.MirrorCS")}),-1.0]])]});
            var Q2;
            Q2=makeQuery(id+"F16.imprint","IMPRINT",FACE,{"disambiguationData":[TD([[makeQuery(id+"F16.imprint","IMPRINT",EDGE,{"derivedFrom":makeQuery(id+"F1.opExtrude","CAP_EDGE",EDGE,{"disambiguationData":[OSD([sQuery(id+"F0.wireOp",EDGE,"E4")])],"isStart":true})}),-1.0]])]});
            var Q3;
            Q3=makeQuery(id+"F16.imprint","IMPRINT",FACE,{"disambiguationData":[TD([[makeQuery(id+"F16.imprint","IMPRINT",EDGE,{"derivedFrom":makeQuery(id+"F1.opExtrude","CAP_EDGE",EDGE,{"disambiguationData":[OSD([sQuery(id+"F0.wireOp",EDGE,"E6")])],"isStart":true})}),-1.0]])]});
            var Q4;
            Q4=makeQuery(id+"F2.opExtrude","CAP_FACE",FACE,{"disambiguationData":[OSD([sQuery(id+"F0.wireOp",EDGE,"E12"),sQuery(id+"F0.wireOp",EDGE,"E13"),sQuery(id+"F0.wireOp",EDGE,"E14"),sQuery(id+"F0.wireOp",EDGE,"E15"),sQuery(id+"F0.wireOp",EDGE,"E17.filletArc"),sQuery(id+"F0.wireOp",EDGE,"E18.filletArc"),sQuery(id+"F0.wireOp",EDGE,"E19.filletArc"),sQuery(id+"F0.wireOp",EDGE,"E20.filletArc"),sQuery(id+"F0.wireOp",EDGE,"E25.0"),sQuery(id+"F0.wireOp",EDGE,"E25.1"),sQuery(id+"F0.wireOp",EDGE,"E25.2"),sQuery(id+"F0.wireOp",EDGE,"E25.3"),sQuery(id+"F0.wireOp",EDGE,"E25.4"),sQuery(id+"F0.wireOp",EDGE,"E25.5"),sQuery(id+"F0.wireOp",EDGE,"E25.6"),sQuery(id+"F0.wireOp",EDGE,"E25.7")])],"isStart":false});
            extrude(context, id + "F17", {"entities" : qUnion([Q0, Q1, Q2, Q3]), "operationType" : NewBodyOperationType.ADD, "endBound" : BoundingType.UP_TO_SURFACE, "endBoundEntityFace" : qUnion([Q4]), "depth" : 25 * mm});
        }
    });
